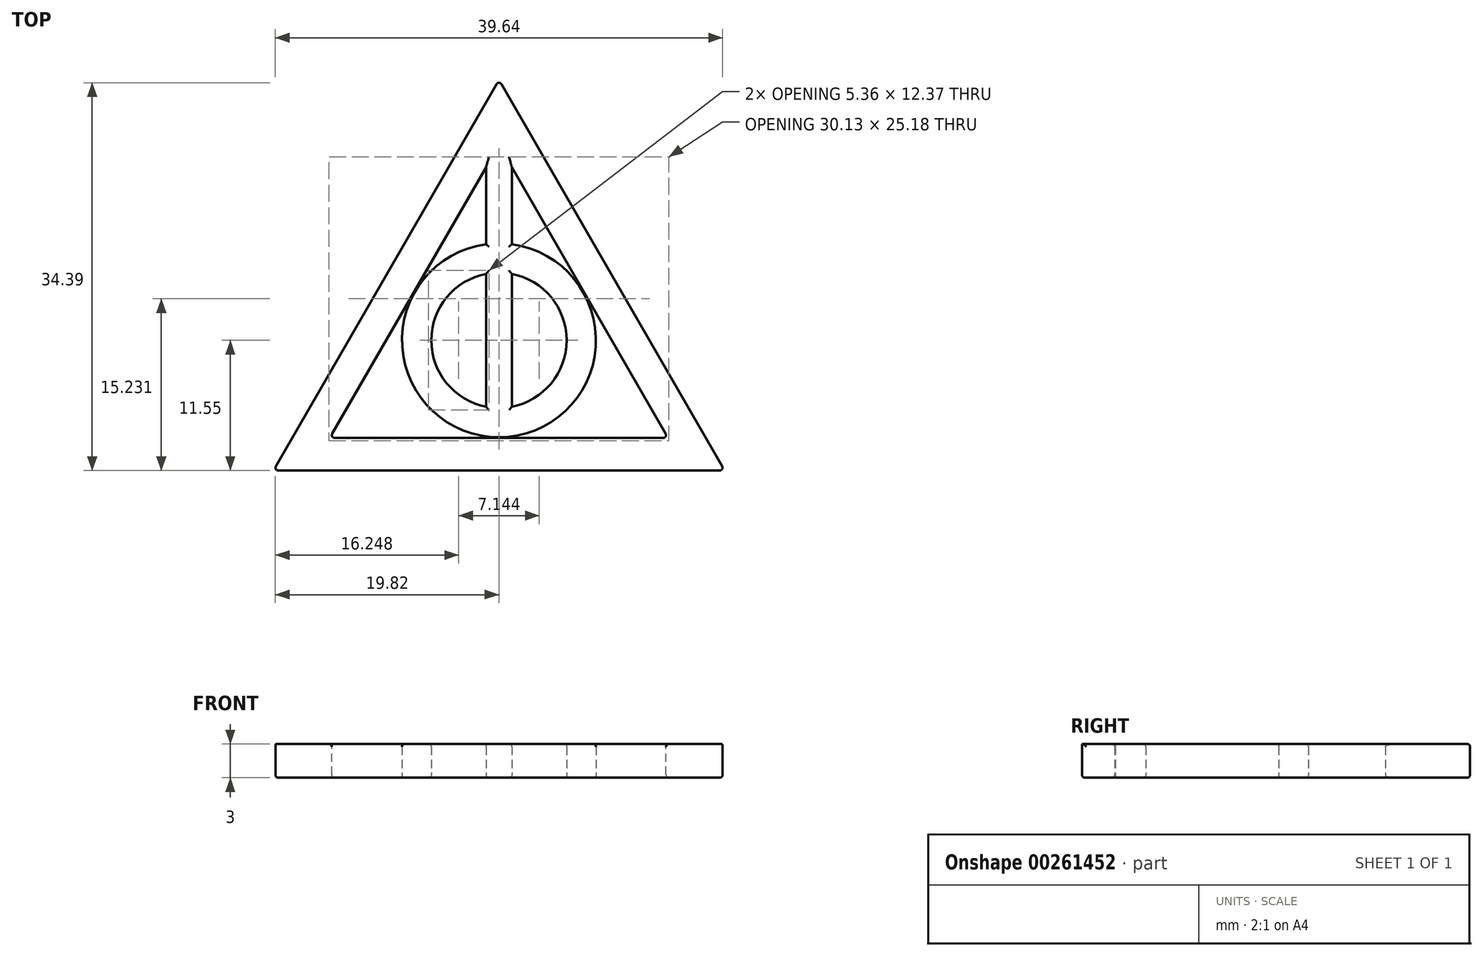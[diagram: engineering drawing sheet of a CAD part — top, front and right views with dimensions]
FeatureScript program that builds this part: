
annotation { "Feature Type Name" : "Feature", "Feature Type Description" : "" }
export const myFeature = defineFeature(function(context is Context, id is Id, definition is map)
    precondition{}
    {
        {
            var Q0;
            Q0=qCreatedBy(makeId("Top.planeOp"),FACE);
            var sketch = newSketch(context, id + "F0", { "sketchPlane" : qUnion([Q0])});
            skCircle(sketch, "E0.cCircle", {"center": v(0, 0) * mm, "radius": 23.1 * mm, "construction": true});
            skLineSegment(sketch, "E0.0", {"start": v(0, 23.1) * mm, "end": v(20, -11.55) * mm});
            skLineSegment(sketch, "E0.1", {"start": v(20, -11.55) * mm, "end": v(-20, -11.55) * mm});
            skLineSegment(sketch, "E0.2", {"start": v(-20, -11.55) * mm, "end": v(0, 23.1) * mm});
            skCircle(sketch, "E1.cCircle", {"center": v(0, 0) * mm, "radius": 17.32 * mm, "construction": true});
            skLineSegment(sketch, "E1.0", {"start": v(0, 17.32) * mm, "end": v(15, -8.66) * mm});
            skLineSegment(sketch, "E1.1", {"start": v(15, -8.66) * mm, "end": v(-15, -8.66) * mm});
            skLineSegment(sketch, "E1.2", {"start": v(-15, -8.66) * mm, "end": v(0, 17.32) * mm});
            skCircle(sketch, "E2", {"center": v(0, 0) * mm, "radius": 8.6 * mm});
            skCircle(sketch, "E3", {"center": v(0, 0) * mm, "radius": 6 * mm});
            skLineSegment(sketch, "E4", {"start": v(-1.14, 15.34) * mm, "end": v(-1.14, -8.66) * mm});
            skLineSegment(sketch, "E5.MirrorCS", {"start": v(1.14, 15.34) * mm, "end": v(1.14, -8.66) * mm});
            skSolve(sketch);
        }
        {
            var Q0;
            Q0=makeQuery(id+"F0.imprint","IMPRINT",FACE,{"disambiguationData":[TD([[makeQuery(id+"F0.imprint","IMPRINT",EDGE,{"derivedFrom":sQuery(id+"F0.wireOp",EDGE,"E0.0")}),-1.0]])]});
            var Q1;
            {var subQ5=sQuery(id+"F0.wireOp",EDGE,"E1.2");var subQ6=sQuery(id+"F0.wireOp",EDGE,"E1.0");var subQ7=makeQuery(id+"F0.imprint","INTERSECT",VERTEX,{"derivedFrom":[subQ6,subQ5]});Q1=makeQuery(id+"F0.imprint","IMPRINT",FACE,{"disambiguationData":[TD([[makeQuery(id+"F0.imprint","IMPRINT",EDGE,{"disambiguationData":[TD([[subQ7,-1.0]])],"derivedFrom":subQ6}),-1.0]])]});}
            var Q2;
            {var subQ0=sQuery(id+"F0.wireOp",EDGE,"E4");var subQ1=sQuery(id+"F0.wireOp",EDGE,"E2");var subQ2=makeQuery(id+"F0.imprint","INTERSECT",VERTEX,{"disambiguationData":[OD(0.0)],"derivedFrom":[subQ1,subQ0]});Q2=makeQuery(id+"F0.imprint","IMPRINT",FACE,{"disambiguationData":[TD([[makeQuery(id+"F0.imprint","IMPRINT",EDGE,{"disambiguationData":[TD([[subQ2,1.0]])],"derivedFrom":subQ1}),1.0]])]});}
            var Q3;
            {var subQ0=sQuery(id+"F0.wireOp",EDGE,"E4");var subQ1=sQuery(id+"F0.wireOp",EDGE,"E2");var subQ2=makeQuery(id+"F0.imprint","INTERSECT",VERTEX,{"disambiguationData":[OD(1.0)],"derivedFrom":[subQ1,subQ0]});Q3=makeQuery(id+"F0.imprint","IMPRINT",FACE,{"disambiguationData":[TD([[makeQuery(id+"F0.imprint","IMPRINT",EDGE,{"disambiguationData":[TD([[subQ2,-1.0]])],"derivedFrom":subQ1}),1.0]])]});}
            var Q4;
            {var subQ0=sQuery(id+"F0.wireOp",EDGE,"E5.MirrorCS");var subQ1=sQuery(id+"F0.wireOp",EDGE,"E2");var subQ2=makeQuery(id+"F0.imprint","INTERSECT",VERTEX,{"disambiguationData":[OD(0.0)],"derivedFrom":[subQ1,subQ0]});Q4=makeQuery(id+"F0.imprint","IMPRINT",FACE,{"disambiguationData":[TD([[makeQuery(id+"F0.imprint","IMPRINT",EDGE,{"disambiguationData":[TD([[subQ2,1.0]])],"derivedFrom":subQ1}),1.0]])]});}
            var Q5;
            {var subQ0=sQuery(id+"F0.wireOp",EDGE,"E4");var subQ1=sQuery(id+"F0.wireOp",EDGE,"E2");var subQ2=makeQuery(id+"F0.imprint","INTERSECT",VERTEX,{"disambiguationData":[OD(0.0)],"derivedFrom":[subQ1,subQ0]});Q5=makeQuery(id+"F0.imprint","IMPRINT",FACE,{"disambiguationData":[TD([[makeQuery(id+"F0.imprint","IMPRINT",EDGE,{"disambiguationData":[TD([[subQ2,-1.0]])],"derivedFrom":subQ1}),1.0]])]});}
            var Q6;
            {var subQ0=sQuery(id+"F0.wireOp",EDGE,"E4");var subQ1=sQuery(id+"F0.wireOp",EDGE,"E3");var subQ2=makeQuery(id+"F0.imprint","INTERSECT",VERTEX,{"disambiguationData":[OD(0.0)],"derivedFrom":[subQ1,subQ0]});Q6=makeQuery(id+"F0.imprint","IMPRINT",FACE,{"disambiguationData":[TD([[makeQuery(id+"F0.imprint","IMPRINT",EDGE,{"disambiguationData":[TD([[subQ2,1.0]])],"derivedFrom":subQ1}),1.0]])]});}
            extrude(context, id + "F1", {"entities" : qUnion([Q0, Q1, Q2, Q3, Q4, Q5, Q6]), "depth" : 3 * mm});
        }
        {
            var Q0;
            Q0=makeQuery(id+"F1.opExtrude","CAP_EDGE",EDGE,{"disambiguationData":[OSD([sQuery(id+"F0.wireOp",EDGE,"E1.1")])],"isStart":true});
            var Q1;
            Q1=makeQuery(id+"F1.opExtrude","CAP_EDGE",EDGE,{"disambiguationData":[OSD([sQuery(id+"F0.wireOp",EDGE,"E1.2")])],"isStart":true});
            var Q2;
            Q2=makeQuery(id+"F1.opExtrude","CAP_EDGE",EDGE,{"disambiguationData":[OSD([sQuery(id+"F0.wireOp",EDGE,"E1.0")])],"isStart":true});
            var Q3;
            {var subQ0=sQuery(id+"F0.wireOp",EDGE,"E5.MirrorCS");Q3=makeQuery(id+"F1.opExtrude","CAP_EDGE",EDGE,{"disambiguationData":[OSD([subQ0]),TDD([makeQuery(id+"F0.imprint","IMPRINT",EDGE,{"disambiguationData":[TD([[makeQuery(id+"F0.imprint","INTERSECT",VERTEX,{"derivedFrom":[sQuery(id+"F0.wireOp",EDGE,"E1.0"),subQ0]}),-1.0]])],"derivedFrom":subQ0})])],"isStart":true});}
            var Q4;
            {var subQ0=sQuery(id+"F0.wireOp",EDGE,"E4");Q4=makeQuery(id+"F1.opExtrude","CAP_EDGE",EDGE,{"disambiguationData":[OSD([subQ0]),TDD([makeQuery(id+"F0.imprint","IMPRINT",EDGE,{"disambiguationData":[TD([[makeQuery(id+"F0.imprint","INTERSECT",VERTEX,{"derivedFrom":[sQuery(id+"F0.wireOp",EDGE,"E1.2"),subQ0]}),-1.0]])],"derivedFrom":subQ0})])],"isStart":true});}
            var Q5;
            Q5=makeQuery(id+"F1.opExtrude","CAP_EDGE",EDGE,{"disambiguationData":[OSD([sQuery(id+"F0.wireOp",EDGE,"E2")])],"isStart":true});
            var Q6;
            Q6=makeQuery(id+"F1.opExtrude","CAP_FACE",FACE,{"disambiguationData":[OSD([sQuery(id+"F0.wireOp",EDGE,"E0.0"),sQuery(id+"F0.wireOp",EDGE,"E0.1"),sQuery(id+"F0.wireOp",EDGE,"E0.2"),sQuery(id+"F0.wireOp",EDGE,"E1.0"),sQuery(id+"F0.wireOp",EDGE,"E1.1"),sQuery(id+"F0.wireOp",EDGE,"E1.2"),sQuery(id+"F0.wireOp",EDGE,"E2"),sQuery(id+"F0.wireOp",EDGE,"E3"),sQuery(id+"F0.wireOp",EDGE,"E4"),sQuery(id+"F0.wireOp",EDGE,"E5.MirrorCS")])],"isStart":true});
            var Q7;
            Q7=makeQuery(id+"F1.opExtrude","SWEPT_EDGE",EDGE,{"disambiguationData":[OSD([sQuery(id+"F0.wireOp",EDGE,"E0.0"),sQuery(id+"F0.wireOp",EDGE,"E0.2")])]});
            var Q8;
            Q8=makeQuery(id+"F1.opExtrude","SWEPT_EDGE",EDGE,{"disambiguationData":[OSD([sQuery(id+"F0.wireOp",EDGE,"E0.0"),sQuery(id+"F0.wireOp",EDGE,"E0.1")])]});
            var Q9;
            Q9=makeQuery(id+"F1.opExtrude","SWEPT_EDGE",EDGE,{"disambiguationData":[OSD([sQuery(id+"F0.wireOp",EDGE,"E0.1"),sQuery(id+"F0.wireOp",EDGE,"E0.2")])]});
            var Q10;
            {var subQ0=sQuery(id+"F0.wireOp",EDGE,"E5.MirrorCS");Q10=makeQuery(id+"F1.opExtrude","CAP_EDGE",EDGE,{"disambiguationData":[OSD([subQ0]),TDD([makeQuery(id+"F0.imprint","IMPRINT",EDGE,{"disambiguationData":[TD([[makeQuery(id+"F0.imprint","INTERSECT",VERTEX,{"derivedFrom":[sQuery(id+"F0.wireOp",EDGE,"E1.0"),subQ0]}),-1.0]])],"derivedFrom":subQ0})])],"isStart":false});}
            var Q11;
            {var subQ0=sQuery(id+"F0.wireOp",EDGE,"E4");Q11=makeQuery(id+"F1.opExtrude","CAP_EDGE",EDGE,{"disambiguationData":[OSD([subQ0]),TDD([makeQuery(id+"F0.imprint","IMPRINT",EDGE,{"disambiguationData":[TD([[makeQuery(id+"F0.imprint","INTERSECT",VERTEX,{"derivedFrom":[sQuery(id+"F0.wireOp",EDGE,"E1.2"),subQ0]}),-1.0]])],"derivedFrom":subQ0})])],"isStart":false});}
            var Q12;
            Q12=makeQuery(id+"F1.opExtrude","CAP_EDGE",EDGE,{"disambiguationData":[OSD([sQuery(id+"F0.wireOp",EDGE,"E1.2")])],"isStart":false});
            var Q13;
            Q13=makeQuery(id+"F1.opExtrude","CAP_EDGE",EDGE,{"disambiguationData":[OSD([sQuery(id+"F0.wireOp",EDGE,"E1.1")])],"isStart":false});
            var Q14;
            Q14=makeQuery(id+"F1.opExtrude","CAP_EDGE",EDGE,{"disambiguationData":[OSD([sQuery(id+"F0.wireOp",EDGE,"E1.0")])],"isStart":false});
            var Q15;
            Q15=makeQuery(id+"F1.opExtrude","SWEPT_EDGE",EDGE,{"disambiguationData":[OSD([sQuery(id+"F0.wireOp",EDGE,"E1.0"),sQuery(id+"F0.wireOp",EDGE,"E1.1")])]});
            var Q16;
            {var subQ0=sQuery(id+"F0.wireOp",EDGE,"E5.MirrorCS");var subQ1=sQuery(id+"F0.wireOp",EDGE,"E3");Q16=makeQuery(id+"F1.opExtrude","CAP_EDGE",EDGE,{"disambiguationData":[OSD([subQ1]),TDD([makeQuery(id+"F0.imprint","IMPRINT",EDGE,{"disambiguationData":[TD([[makeQuery(id+"F0.imprint","INTERSECT",VERTEX,{"disambiguationData":[OD(0.0)],"derivedFrom":[subQ1,subQ0]}),1.0]])],"derivedFrom":subQ1})])],"isStart":false});}
            var Q17;
            {var subQ0=sQuery(id+"F0.wireOp",EDGE,"E4");var subQ1=sQuery(id+"F0.wireOp",EDGE,"E3");Q17=makeQuery(id+"F1.opExtrude","CAP_EDGE",EDGE,{"disambiguationData":[OSD([subQ1]),TDD([makeQuery(id+"F0.imprint","IMPRINT",EDGE,{"disambiguationData":[TD([[makeQuery(id+"F0.imprint","INTERSECT",VERTEX,{"disambiguationData":[OD(0.0)],"derivedFrom":[subQ1,subQ0]}),-1.0]])],"derivedFrom":subQ1})])],"isStart":false});}
            var Q18;
            {var subQ0=sQuery(id+"F0.wireOp",EDGE,"E4");var subQ1=sQuery(id+"F0.wireOp",EDGE,"E3");Q18=makeQuery(id+"F1.opExtrude","CAP_EDGE",EDGE,{"disambiguationData":[OSD([subQ0]),TDD([makeQuery(id+"F0.imprint","IMPRINT",EDGE,{"disambiguationData":[TD([[makeQuery(id+"F0.imprint","INTERSECT",VERTEX,{"disambiguationData":[OD(0.0)],"derivedFrom":[subQ1,subQ0]}),-1.0]])],"derivedFrom":subQ0})])],"isStart":false});}
            var Q19;
            {var subQ0=sQuery(id+"F0.wireOp",EDGE,"E5.MirrorCS");var subQ1=sQuery(id+"F0.wireOp",EDGE,"E3");Q19=makeQuery(id+"F1.opExtrude","CAP_EDGE",EDGE,{"disambiguationData":[OSD([subQ0]),TDD([makeQuery(id+"F0.imprint","IMPRINT",EDGE,{"disambiguationData":[TD([[makeQuery(id+"F0.imprint","INTERSECT",VERTEX,{"disambiguationData":[OD(0.0)],"derivedFrom":[subQ1,subQ0]}),-1.0]])],"derivedFrom":subQ0})])],"isStart":false});}
            var Q20;
            Q20=makeQuery(id+"F1.opExtrude","CAP_EDGE",EDGE,{"disambiguationData":[OSD([sQuery(id+"F0.wireOp",EDGE,"E0.2")])],"isStart":false});
            var Q21;
            Q21=makeQuery(id+"F1.opExtrude","CAP_EDGE",EDGE,{"disambiguationData":[OSD([sQuery(id+"F0.wireOp",EDGE,"E0.0")])],"isStart":false});
            var Q22;
            Q22=makeQuery(id+"F1.opExtrude","SWEPT_EDGE",EDGE,{"disambiguationData":[OSD([sQuery(id+"F0.wireOp",EDGE,"E1.1"),sQuery(id+"F0.wireOp",EDGE,"E1.2")])]});
            var Q23;
            Q23=makeQuery(id+"F1.opExtrude","CAP_EDGE",EDGE,{"disambiguationData":[OSD([sQuery(id+"F0.wireOp",EDGE,"E2")])],"isStart":false});
            fillet(context, id + "F2", {"entities" : qUnion([Q0, Q1, Q2, Q3, Q4, Q5, Q6, Q7, Q8, Q9, Q10, Q11, Q12, Q13, Q14, Q15, Q16, Q17, Q18, Q19, Q20, Q21, Q22, Q23]), "radius" : .25 * mm, "tangentPropagation" : true, "allowEdgeOverflow" : false});
        }
    });
